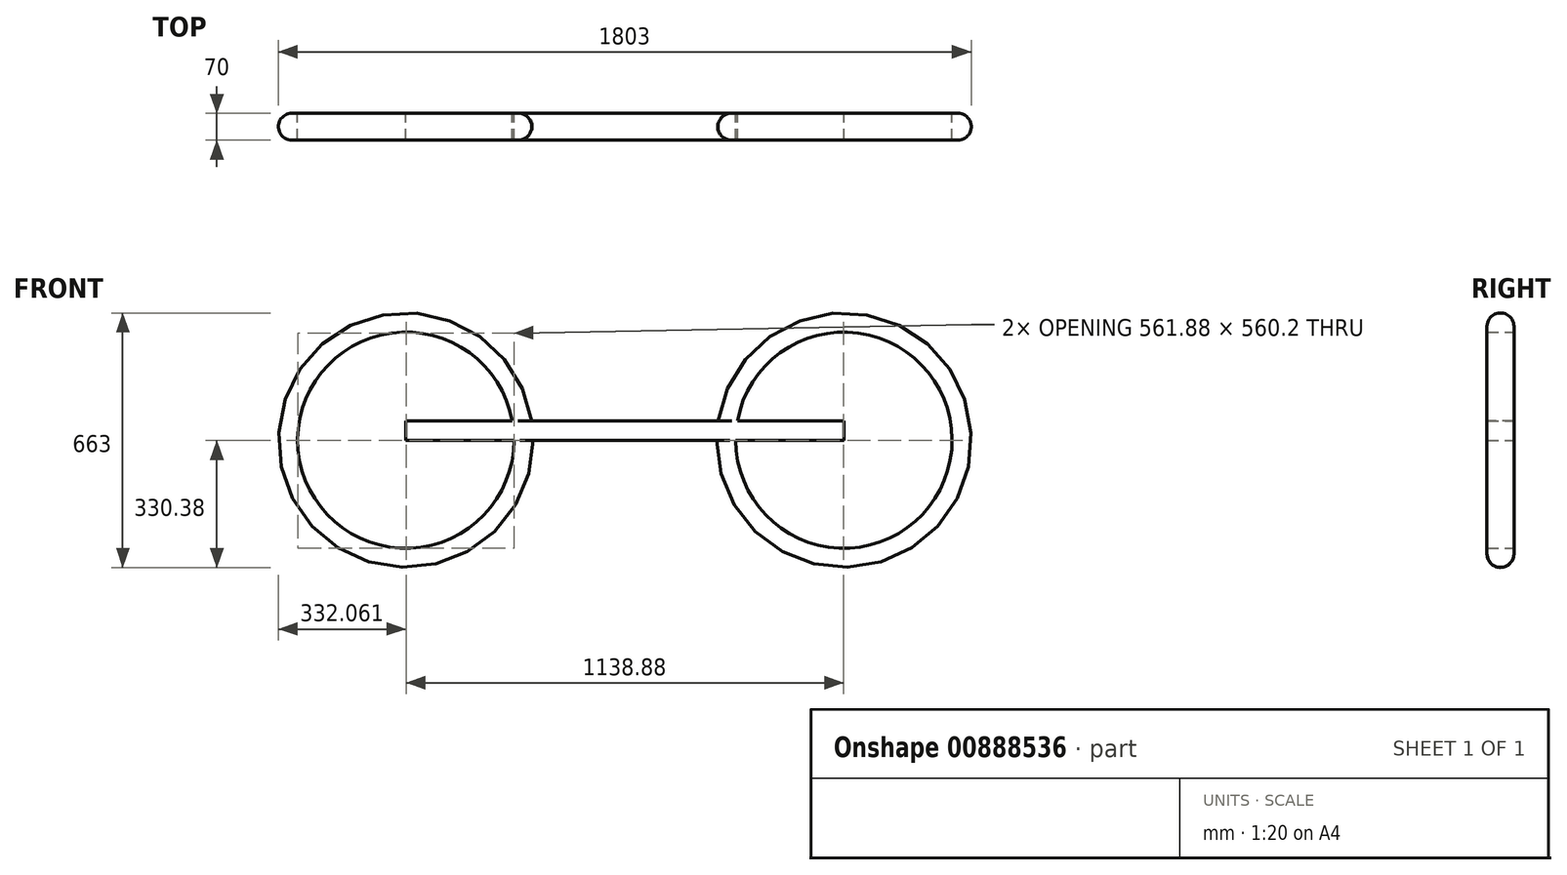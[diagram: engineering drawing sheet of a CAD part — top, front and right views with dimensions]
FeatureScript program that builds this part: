
annotation { "Feature Type Name" : "Feature", "Feature Type Description" : "" }
export const myFeature = defineFeature(function(context is Context, id is Id, definition is map)
    precondition{}
    {
        {
            var Q0;
            Q0=qCreatedBy(makeId("Front.planeOp"),FACE);
            var sketch = newSketch(context, id + "F0", { "sketchPlane" : qUnion([Q0])});
            skCircle(sketch, "E0", {"center": v(0, 0) * mm, "radius": 331.5 * mm});
            skCircle(sketch, "E1.0", {"center": v(0, 0) * mm, "radius": 281.5 * mm});
            skSolve(sketch);
        }
        {
            var Q0;
            Q0 = qSketchRegion(id + "F0", true);
            extrude(context, id + "F1", {"entities" : qUnion([Q0]), "depth" : 70 * mm, "offsetDistance" : 25 * mm});
        }
        {
            var Q0;
            Q0=makeQuery(id+"F1.opExtrude","CAP_EDGE",EDGE,{"disambiguationData":[OSD([sQuery(id+"F0.wireOp",EDGE,"E0")])],"isStart":false});
            var Q1;
            Q1=makeQuery(id+"F1.opExtrude","CAP_EDGE",EDGE,{"disambiguationData":[OSD([sQuery(id+"F0.wireOp",EDGE,"E0")])],"isStart":true});
            fillet(context, id + "F2", {"entities" : qUnion([Q0, Q1]), "radius" : 35 * mm, "tangentPropagation" : true, "allowEdgeOverflow" : false});
        }
        {
            var Q0;
            Q0=makeQuery(id+"F1.opExtrude","SWEPT_BODY",BODY,{"disambiguationData":[OSD([sQuery(id+"F0.wireOp",EDGE,"E0"),sQuery(id+"F0.wireOp",EDGE,"E1.0")])]});
            transform(context, id + "F3", {"entities" : qUnion([Q0]), "transformType" : TransformType.TRANSLATION_3D, "dx" : 1140 * mm, "dy" : 0 * mm, "dz" : 0 * mm, "makeCopy" : true});
        }
        {
            var Q0;
            Q0=qCreatedBy(makeId("Front.planeOp"),FACE);
            var sketch = newSketch(context, id + "F4", { "sketchPlane" : qUnion([Q0])});
            skLineSegment(sketch, "E2.bottom", {"start": v(0, 0) * mm, "end": v(1140, 0) * mm});
            skLineSegment(sketch, "E2.top", {"start": v(0, 50) * mm, "end": v(1140, 50) * mm});
            skLineSegment(sketch, "E2.left", {"start": v(0, 0) * mm, "end": v(0, 50) * mm});
            skLineSegment(sketch, "E2.right", {"start": v(1140, 0) * mm, "end": v(1140, 50) * mm});
            skSolve(sketch);
        }
        {
            var Q0;
            Q0 = qSketchRegion(id + "F4", true);
            extrude(context, id + "F5", {"entities" : qUnion([Q0]), "operationType" : NewBodyOperationType.ADD, "depth" : 70 * mm, "offsetDistance" : 25 * mm});
        }
    });
